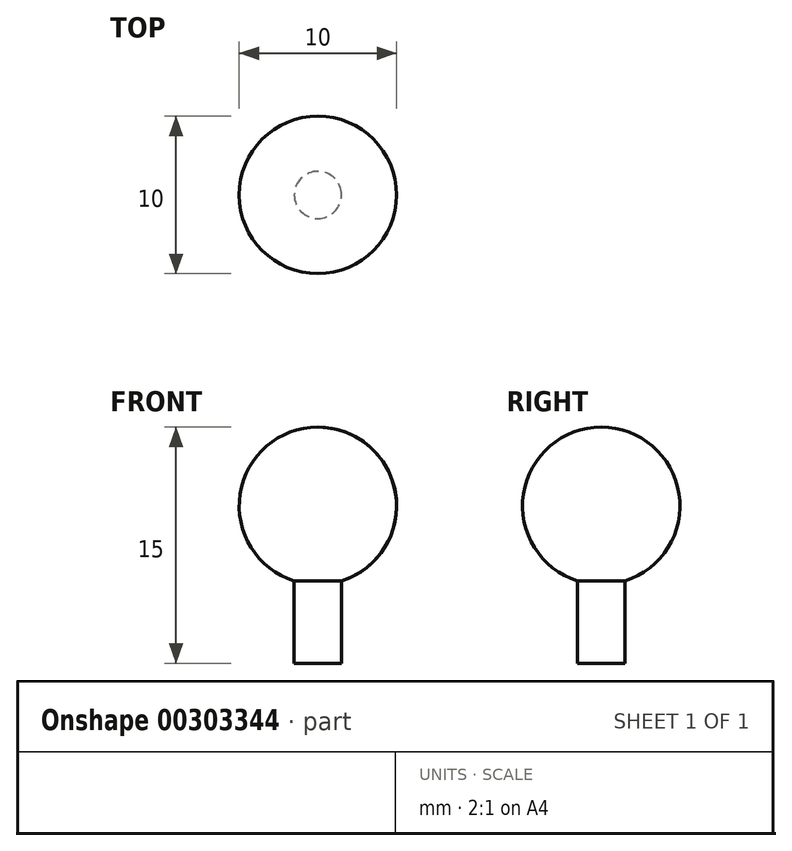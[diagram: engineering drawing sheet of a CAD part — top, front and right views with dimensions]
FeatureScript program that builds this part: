
annotation { "Feature Type Name" : "Feature", "Feature Type Description" : "" }
export const myFeature = defineFeature(function(context is Context, id is Id, definition is map)
    precondition{}
    {
        {
            var Q0;
            Q0=qCreatedBy(makeId("Front.planeOp"),FACE);
            var sketch = newSketch(context, id + "F0", { "sketchPlane" : qUnion([Q0])});
            skArc(sketch, "E0", {"start": v(1.5, -4.77) * mm, "mid": v(4.94, 0.76) * mm, "end": v(0, 5) * mm});
            skLineSegment(sketch, "E1.top", {"start": v(1.5, -10) * mm, "end": v(0, -10) * mm});
            skLineSegment(sketch, "E1.left", {"start": v(1.5, -4.77) * mm, "end": v(1.5, -10) * mm});
            skPoint(sketch, "E1.bottom.start.orphan", {"position": v(1.5, 10) * mm});
            skPoint(sketch, "E2.orphan", {"position": v(-1.5, 10) * mm});
            skLineSegment(sketch, "E3", {"start": v(0, 5) * mm, "end": v(0, -10) * mm});
            skPoint(sketch, "E4.orphan", {"position": v(-1.5, -10) * mm});
            skSolve(sketch);
        }
        {
            var Q0;
            Q0=makeQuery(id+"F0.imprint","IMPRINT",FACE,{"disambiguationData":[TD([[makeQuery(id+"F0.imprint","IMPRINT",EDGE,{"derivedFrom":sQuery(id+"F0.wireOp",EDGE,"E0")}),1.0]])]});
            var Q1;
            Q1=sQuery(id+"F0.wireOp",EDGE,"E3");
            revolve(context, id + "F1", {"entities" : qUnion([Q0]), "axis" : qUnion([Q1]), "revolveType" : RevolveType.FULL});
        }
    });
